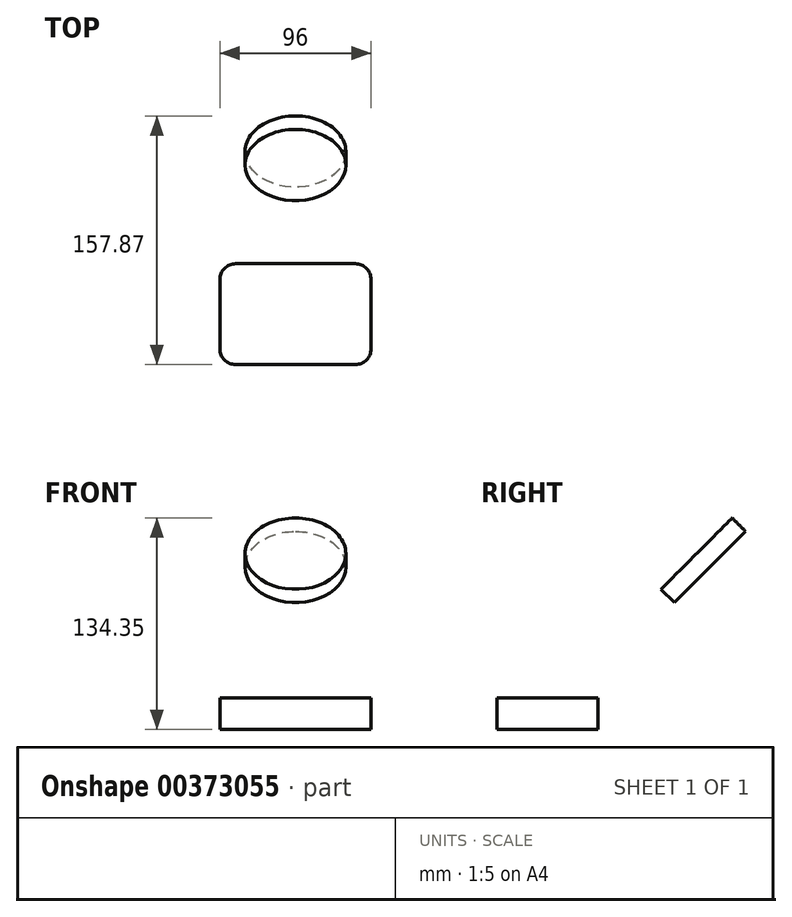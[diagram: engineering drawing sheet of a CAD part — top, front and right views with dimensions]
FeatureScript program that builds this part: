
annotation { "Feature Type Name" : "Feature", "Feature Type Description" : "" }
export const myFeature = defineFeature(function(context is Context, id is Id, definition is map)
    precondition{}
    {
        {
            var Q0;
            Q0=qCreatedBy(makeId("Top.planeOp"),FACE);
            var sketch = newSketch(context, id + "F0", { "sketchPlane" : qUnion([Q0])});
            skLineSegment(sketch, "E0.bottom", {"start": v(48, -32) * mm, "end": v(-48, -32) * mm});
            skLineSegment(sketch, "E0.top", {"start": v(48, 32) * mm, "end": v(-48, 32) * mm});
            skLineSegment(sketch, "E0.left", {"start": v(48, -32) * mm, "end": v(48, 32) * mm});
            skLineSegment(sketch, "E0.right", {"start": v(-48, -32) * mm, "end": v(-48, 32) * mm});
            skPoint(sketch, "E0.middle", {"position": v(0, 0) * mm});
            skSolve(sketch);
        }
        {
            var Q0;
            Q0=makeQuery(id+"F0.imprint","IMPRINT",FACE,{"disambiguationData":[TD([[makeQuery(id+"F0.imprint","IMPRINT",EDGE,{"derivedFrom":sQuery(id+"F0.wireOp",EDGE,"E0.bottom")}),-1.0]])]});
            extrude(context, id + "F1", {"entities" : qUnion([Q0]), "depth" : 20 * mm});
        }
        {
            var Q0;
            Q0=makeQuery(id+"F1.opExtrude","SWEPT_EDGE",EDGE,{"disambiguationData":[OSD([sQuery(id+"F0.wireOp",EDGE,"E0.bottom"),sQuery(id+"F0.wireOp",EDGE,"E0.right")])]});
            var Q1;
            Q1=makeQuery(id+"F1.opExtrude","SWEPT_EDGE",EDGE,{"disambiguationData":[OSD([sQuery(id+"F0.wireOp",EDGE,"E0.bottom"),sQuery(id+"F0.wireOp",EDGE,"E0.left")])]});
            var Q2;
            Q2=makeQuery(id+"F1.opExtrude","SWEPT_EDGE",EDGE,{"disambiguationData":[OSD([sQuery(id+"F0.wireOp",EDGE,"E0.top"),sQuery(id+"F0.wireOp",EDGE,"E0.left")])]});
            var Q3;
            Q3=makeQuery(id+"F1.opExtrude","SWEPT_EDGE",EDGE,{"disambiguationData":[OSD([sQuery(id+"F0.wireOp",EDGE,"E0.top"),sQuery(id+"F0.wireOp",EDGE,"E0.right")])]});
            fillet(context, id + "F2", {"entities" : qUnion([Q0, Q1, Q2, Q3]), "radius" : 10 * mm, "tangentPropagation" : true, "allowEdgeOverflow" : false});
        }
        {
            var Q0;
            Q0=qCreatedBy(makeId("Right.planeOp"),FACE);
            var sketch = newSketch(context, id + "F3", { "sketchPlane" : qUnion([Q0])});
            skLineSegment(sketch, "E1", {"start": v(0, 0) * mm, "end": v(87.52, 87.52) * mm});
            skSolve(sketch);
        }
        {
            var Q0;
            Q0=qCreatedBy(makeId("Front.planeOp"),FACE);
            var Q1;
            Q1=sQuery(id+"F3.wireOp",EDGE,"E1");
            cPlane(context, id + "F4", {"entities" : qUnion([Q0, Q1]), "cplaneType" : CPlaneType.LINE_ANGLE, "offset" : 25 * mm, "angle" : 0 * degree, "width" : 150 * mm, "height" : 150 * mm});
        }
        {
            var Q0;
            Q0=qCreatedBy(id+"F4.planeOp",FACE);
            var sketch = newSketch(context, id + "F5", { "sketchPlane" : qUnion([Q0])});
            skCircle(sketch, "E2", {"center": v(0, 146) * mm, "radius": 32 * mm});
            skSolve(sketch);
        }
        {
            var Q0;
            Q0=makeQuery(id+"F5.imprint","IMPRINT",FACE,{"disambiguationData":[TD([[makeQuery(id+"F5.imprint","IMPRINT",EDGE,{"derivedFrom":sQuery(id+"F5.wireOp",EDGE,"E2")}),1.0]])]});
            extrude(context, id + "F6", {"entities" : qUnion([Q0]), "oppositeDirection" : true, "depth" : 12 * mm});
        }
    });
